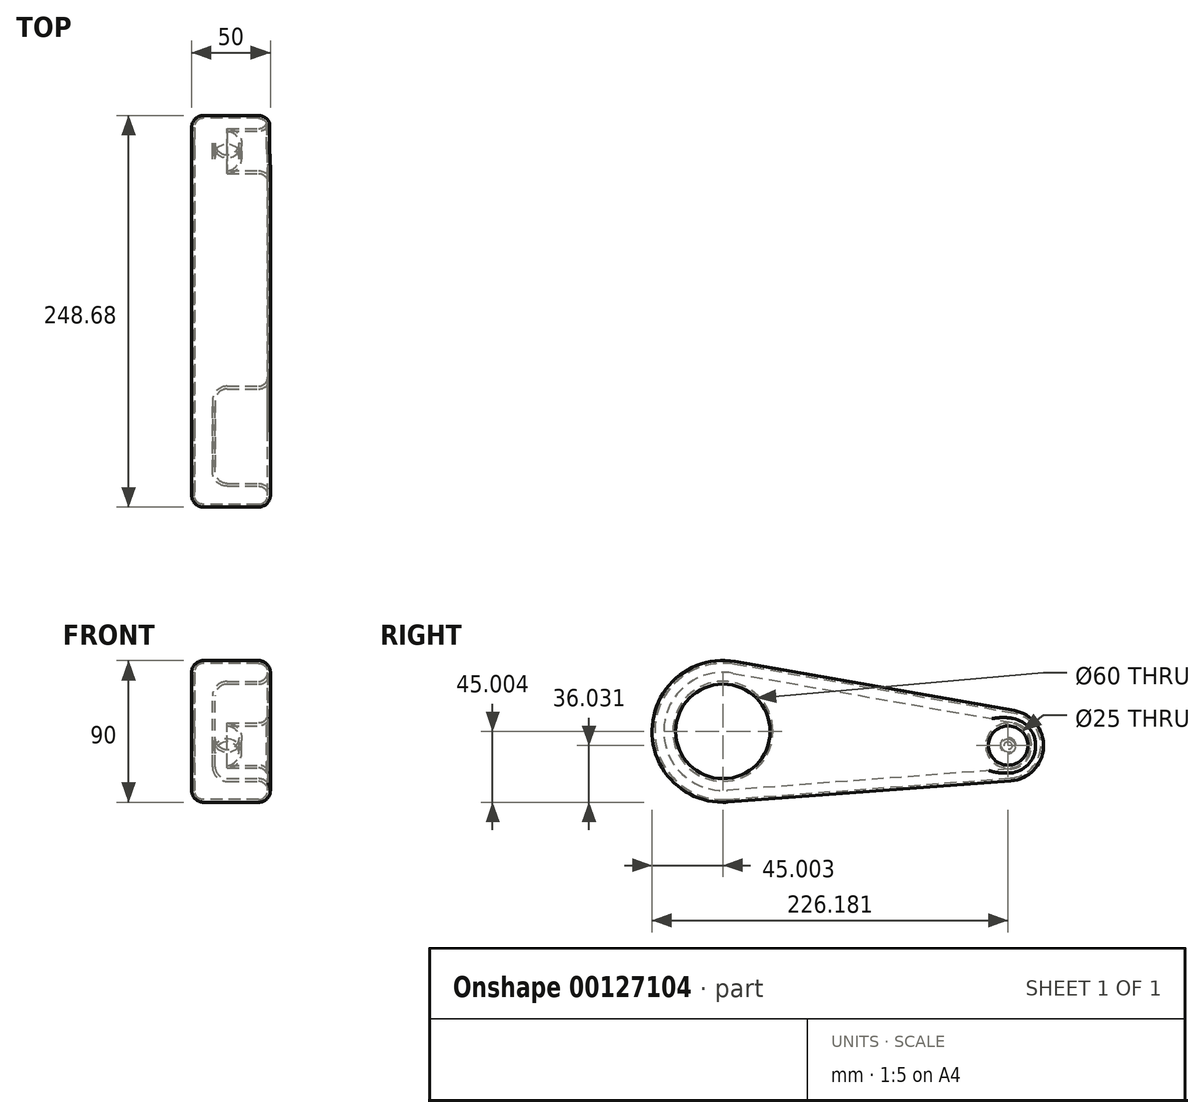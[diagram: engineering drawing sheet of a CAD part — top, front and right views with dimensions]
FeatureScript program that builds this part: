
annotation { "Feature Type Name" : "Feature", "Feature Type Description" : "" }
export const myFeature = defineFeature(function(context is Context, id is Id, definition is map)
    precondition{}
    {
        {
            var Q0;
            Q0=qCreatedBy(makeId("Right.planeOp"),FACE);
            var sketch = newSketch(context, id + "F0", { "sketchPlane" : qUnion([Q0])});
            skCircle(sketch, "E0", {"center": v(-59.15, 23.6) * mm, "radius": 45 * mm});
            skCircle(sketch, "E1", {"center": v(122.03, 14.62) * mm, "radius": 22.5 * mm});
            skLineSegment(sketch, "E2", {"start": v(123.71, -7.82) * mm, "end": v(-55.78, -21.28) * mm});
            skLineSegment(sketch, "E3", {"start": v(-51.36, 67.92) * mm, "end": v(125.92, 36.78) * mm});
            skSolve(sketch);
        }
        {
            var Q0;
            {var subQ0=sQuery(id+"F0.wireOp",EDGE,"E0");var subQ1=makeQuery(id+"F0.imprint","INTERSECT",VERTEX,{"derivedFrom":[subQ0,sQuery(id+"F0.wireOp",EDGE,"E2")]});Q0=makeQuery(id+"F0.imprint","IMPRINT",FACE,{"disambiguationData":[TD([[makeQuery(id+"F0.imprint","IMPRINT",EDGE,{"disambiguationData":[TD([[subQ1,1.0]])],"derivedFrom":subQ0}),1.0]])]});}
            var Q1;
            {var subQ0=sQuery(id+"F0.wireOp",EDGE,"E2");Q1=makeQuery(id+"F0.imprint","IMPRINT",FACE,{"disambiguationData":[TD([[makeQuery(id+"F0.imprint","IMPRINT",EDGE,{"derivedFrom":subQ0}),-1.0]])]});}
            var Q2;
            {var subQ0=sQuery(id+"F0.wireOp",EDGE,"E1");var subQ1=makeQuery(id+"F0.imprint","INTERSECT",VERTEX,{"derivedFrom":[subQ0,sQuery(id+"F0.wireOp",EDGE,"E2")]});Q2=makeQuery(id+"F0.imprint","IMPRINT",FACE,{"disambiguationData":[TD([[makeQuery(id+"F0.imprint","IMPRINT",EDGE,{"disambiguationData":[TD([[subQ1,1.0]])],"derivedFrom":subQ0}),1.0]])]});}
            var Q3;
            Q3=sQuery(id+"F0.wireOp",EDGE,"E0");
            extrude(context, id + "F1", {"entities" : qUnion([Q0, Q1, Q2]), "surfaceEntities" : qUnion([Q3]), "depth" : 50 * mm});
        }
        {
            var Q0;
            Q0=makeQuery(id+"F1.opExtrude","CAP_FACE",FACE,{"disambiguationData":[OSD([sQuery(id+"F0.wireOp",EDGE,"E0"),sQuery(id+"F0.wireOp",EDGE,"E1"),sQuery(id+"F0.wireOp",EDGE,"E2"),sQuery(id+"F0.wireOp",EDGE,"E3")])],"isStart":false});
            var sketch = newSketch(context, id + "F2", { "sketchPlane" : qUnion([Q0])});
            skCircle(sketch, "E4", {"center": v(-59.15, 23.6) * mm, "radius": 30 * mm});
            skCircle(sketch, "E5", {"center": v(122.03, 14.62) * mm, "radius": 12.5 * mm});
            skSolve(sketch);
        }
        {
            var Q0;
            Q0=makeQuery(id+"F2.imprint","IMPRINT",FACE,{"disambiguationData":[TD([[makeQuery(id+"F2.imprint","IMPRINT",EDGE,{"derivedFrom":sQuery(id+"F2.wireOp",EDGE,"E4")}),1.0]])]});
            var Q1;
            Q1=makeQuery(id+"F2.imprint","IMPRINT",FACE,{"disambiguationData":[TD([[makeQuery(id+"F2.imprint","IMPRINT",EDGE,{"derivedFrom":sQuery(id+"F2.wireOp",EDGE,"E5")}),1.0]])]});
            extrude(context, id + "F3", {"entities" : qUnion([Q0, Q1]), "operationType" : NewBodyOperationType.REMOVE, "oppositeDirection" : true, "depth" : 35 * mm});
        }
        {
            var Q0;
            Q0=makeQuery(id+"F1.opExtrude","CAP_FACE",FACE,{"disambiguationData":[OSD([sQuery(id+"F0.wireOp",EDGE,"E0"),sQuery(id+"F0.wireOp",EDGE,"E1"),sQuery(id+"F0.wireOp",EDGE,"E2"),sQuery(id+"F0.wireOp",EDGE,"E3")])],"isStart":false});
            var Q1;
            Q1=makeQuery(id+"F1.opExtrude","CAP_EDGE",EDGE,{"disambiguationData":[OSD([sQuery(id+"F0.wireOp",EDGE,"E3")])],"isStart":false});
            var Q2;
            Q2=makeQuery(id+"F1.opExtrude","CAP_EDGE",EDGE,{"disambiguationData":[OSD([sQuery(id+"F0.wireOp",EDGE,"E2")])],"isStart":true});
            var Q3;
            Q3=makeQuery(id+"F3.boolean.opBoolean","COPY",EDGE,{"derivedFrom":makeQuery(id+"F3.opExtrude","CAP_EDGE",EDGE,{"disambiguationData":[OSD([sQuery(id+"F2.wireOp",EDGE,"E4")])],"isStart":false})});
            var Q4;
            Q4=makeQuery(id+"F3.boolean.opBoolean","COPY",EDGE,{"derivedFrom":makeQuery(id+"F3.opExtrude","CAP_EDGE",EDGE,{"disambiguationData":[OSD([sQuery(id+"F2.wireOp",EDGE,"E5")])],"isStart":false})});
            fillet(context, id + "F4", {"entities" : qUnion([Q0, Q1, Q2, Q3, Q4]), "radius" : 7.5 * mm, "tangentPropagation" : true, "allowEdgeOverflow" : false});
        }
        {
            var Q0;
            Q0=makeQuery(id+"F1.opExtrude","CAP_FACE",FACE,{"disambiguationData":[OSD([sQuery(id+"F0.wireOp",EDGE,"E0"),sQuery(id+"F0.wireOp",EDGE,"E1"),sQuery(id+"F0.wireOp",EDGE,"E2"),sQuery(id+"F0.wireOp",EDGE,"E3")])],"isStart":true});
            shell(context, id + "F5", {"entities" : qUnion([Q0]), "thickness" : 1.75 * mm});
        }
    });
